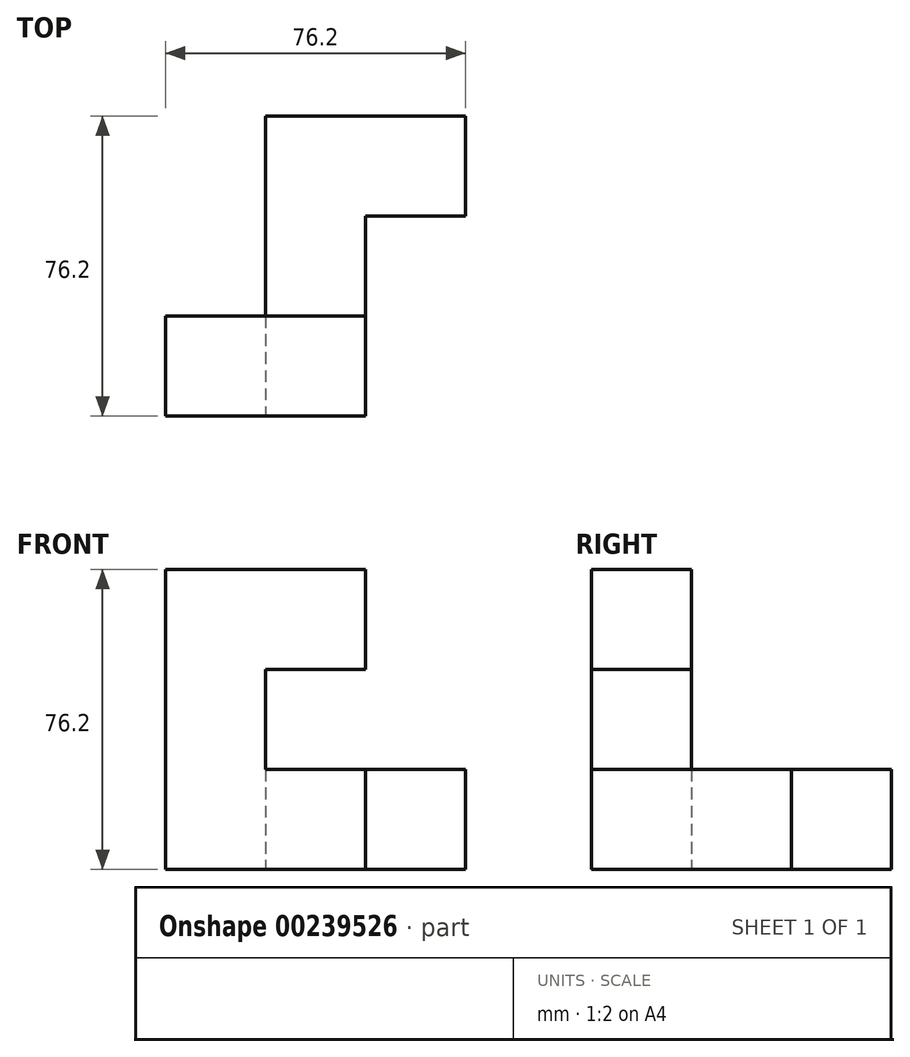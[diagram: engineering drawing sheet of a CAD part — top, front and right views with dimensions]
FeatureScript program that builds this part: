
annotation { "Feature Type Name" : "Feature", "Feature Type Description" : "" }
export const myFeature = defineFeature(function(context is Context, id is Id, definition is map)
    precondition{}
    {
        {
            var Q0;
            Q0=qCreatedBy(makeId("Front.planeOp"),FACE);
            var sketch = newSketch(context, id + "F0", { "sketchPlane" : qUnion([Q0])});
            skLineSegment(sketch, "E0.bottom", {"start": v(-12.7, 12.7) * mm, "end": v(12.7, 12.7) * mm});
            skLineSegment(sketch, "E0.top", {"start": v(-12.7, -12.7) * mm, "end": v(12.7, -12.7) * mm});
            skLineSegment(sketch, "E0.left", {"start": v(-12.7, 12.7) * mm, "end": v(-12.7, -12.7) * mm});
            skLineSegment(sketch, "E0.right", {"start": v(12.7, 12.7) * mm, "end": v(12.7, -12.7) * mm});
            skPoint(sketch, "E0.middle", {"position": v(0, 0) * mm});
            skSolve(sketch);
        }
        {
            var Q0;
            Q0 = qSketchRegion(id + "F0", true);
            extrude(context, id + "F1", {"entities" : qUnion([Q0]), "endBound" : BoundingType.SYMMETRIC, "depth" : 76.2 * mm});
        }
        {
            var Q0;
            Q0=qCreatedBy(makeId("Right.planeOp"),FACE);
            var sketch = newSketch(context, id + "F2", { "sketchPlane" : qUnion([Q0])});
            skLineSegment(sketch, "E1.bottom", {"start": v(38.1, 12.7) * mm, "end": v(12.7, 12.7) * mm});
            skLineSegment(sketch, "E1.top", {"start": v(38.1, -12.7) * mm, "end": v(12.7, -12.7) * mm});
            skLineSegment(sketch, "E1.left", {"start": v(38.1, 12.7) * mm, "end": v(38.1, -12.7) * mm});
            skLineSegment(sketch, "E1.right", {"start": v(12.7, 12.7) * mm, "end": v(12.7, -12.7) * mm});
            skSolve(sketch);
        }
        {
            var Q0;
            Q0 = qSketchRegion(id + "F2", true);
            extrude(context, id + "F3", {"entities" : qUnion([Q0]), "operationType" : NewBodyOperationType.ADD, "depth" : 38.1 * mm});
        }
        {
            var Q0;
            Q0=makeQuery(id+"F1.opExtrude","SWEPT_FACE",FACE,{"disambiguationData":[OSD([sQuery(id+"F0.wireOp",EDGE,"E0.left")])]});
            var sketch = newSketch(context, id + "F4", { "sketchPlane" : qUnion([Q0])});
            skLineSegment(sketch, "E2.bottom", {"start": v(38.1, 12.7) * mm, "end": v(12.7, 12.7) * mm});
            skLineSegment(sketch, "E2.top", {"start": v(38.1, -12.7) * mm, "end": v(12.7, -12.7) * mm});
            skLineSegment(sketch, "E2.left", {"start": v(38.1, 12.7) * mm, "end": v(38.1, -12.7) * mm});
            skLineSegment(sketch, "E2.right", {"start": v(12.7, 12.7) * mm, "end": v(12.7, -12.7) * mm});
            skSolve(sketch);
        }
        {
            var Q0;
            Q0 = qSketchRegion(id + "F4", true);
            extrude(context, id + "F5", {"entities" : qUnion([Q0]), "operationType" : NewBodyOperationType.ADD, "depth" : 25.4 * mm});
        }
        {
            var Q0;
            Q0=makeQuery(id+"F5.boolean.opBoolean","MERGE",FACE,{"derivedFrom":[makeQuery(id+"F3.boolean.opBoolean","MERGE",FACE,{"derivedFrom":[makeQuery(id+"F1.opExtrude","SWEPT_FACE",FACE,{"disambiguationData":[OSD([sQuery(id+"F0.wireOp",EDGE,"E0.bottom")])]}),makeQuery(id+"F3.opExtrude","SWEPT_FACE",FACE,{"disambiguationData":[OSD([sQuery(id+"F2.wireOp",EDGE,"E1.bottom")])]})]}),makeQuery(id+"F5.opExtrude","SWEPT_FACE",FACE,{"disambiguationData":[OSD([sQuery(id+"F4.wireOp",EDGE,"E2.bottom")])]})]});
            var sketch = newSketch(context, id + "F6", { "sketchPlane" : qUnion([Q0])});
            skLineSegment(sketch, "E3.bottom", {"start": v(-38.1, -12.7) * mm, "end": v(-12.7, -12.7) * mm});
            skLineSegment(sketch, "E3.top", {"start": v(-38.1, -38.1) * mm, "end": v(-12.7, -38.1) * mm});
            skLineSegment(sketch, "E3.left", {"start": v(-38.1, -12.7) * mm, "end": v(-38.1, -38.1) * mm});
            skLineSegment(sketch, "E3.right", {"start": v(-12.7, -12.7) * mm, "end": v(-12.7, -38.1) * mm});
            skSolve(sketch);
        }
        {
            var Q0;
            Q0 = qSketchRegion(id + "F6", true);
            extrude(context, id + "F7", {"entities" : qUnion([Q0]), "operationType" : NewBodyOperationType.ADD, "depth" : 50.8 * mm});
        }
        {
            var Q0;
            Q0=makeQuery(id+"F7.opExtrude","SWEPT_FACE",FACE,{"disambiguationData":[OSD([sQuery(id+"F6.wireOp",EDGE,"E3.right")])]});
            var sketch = newSketch(context, id + "F8", { "sketchPlane" : qUnion([Q0])});
            skLineSegment(sketch, "E4.bottom", {"start": v(-38.1, 63.5) * mm, "end": v(-12.7, 63.5) * mm});
            skLineSegment(sketch, "E4.top", {"start": v(-38.1, 38.1) * mm, "end": v(-12.7, 38.1) * mm});
            skLineSegment(sketch, "E4.left", {"start": v(-38.1, 63.5) * mm, "end": v(-38.1, 38.1) * mm});
            skLineSegment(sketch, "E4.right", {"start": v(-12.7, 63.5) * mm, "end": v(-12.7, 38.1) * mm});
            skSolve(sketch);
        }
        {
            var Q0;
            Q0 = qSketchRegion(id + "F8", true);
            extrude(context, id + "F9", {"entities" : qUnion([Q0]), "operationType" : NewBodyOperationType.ADD, "depth" : 25.4 * mm});
        }
    });
